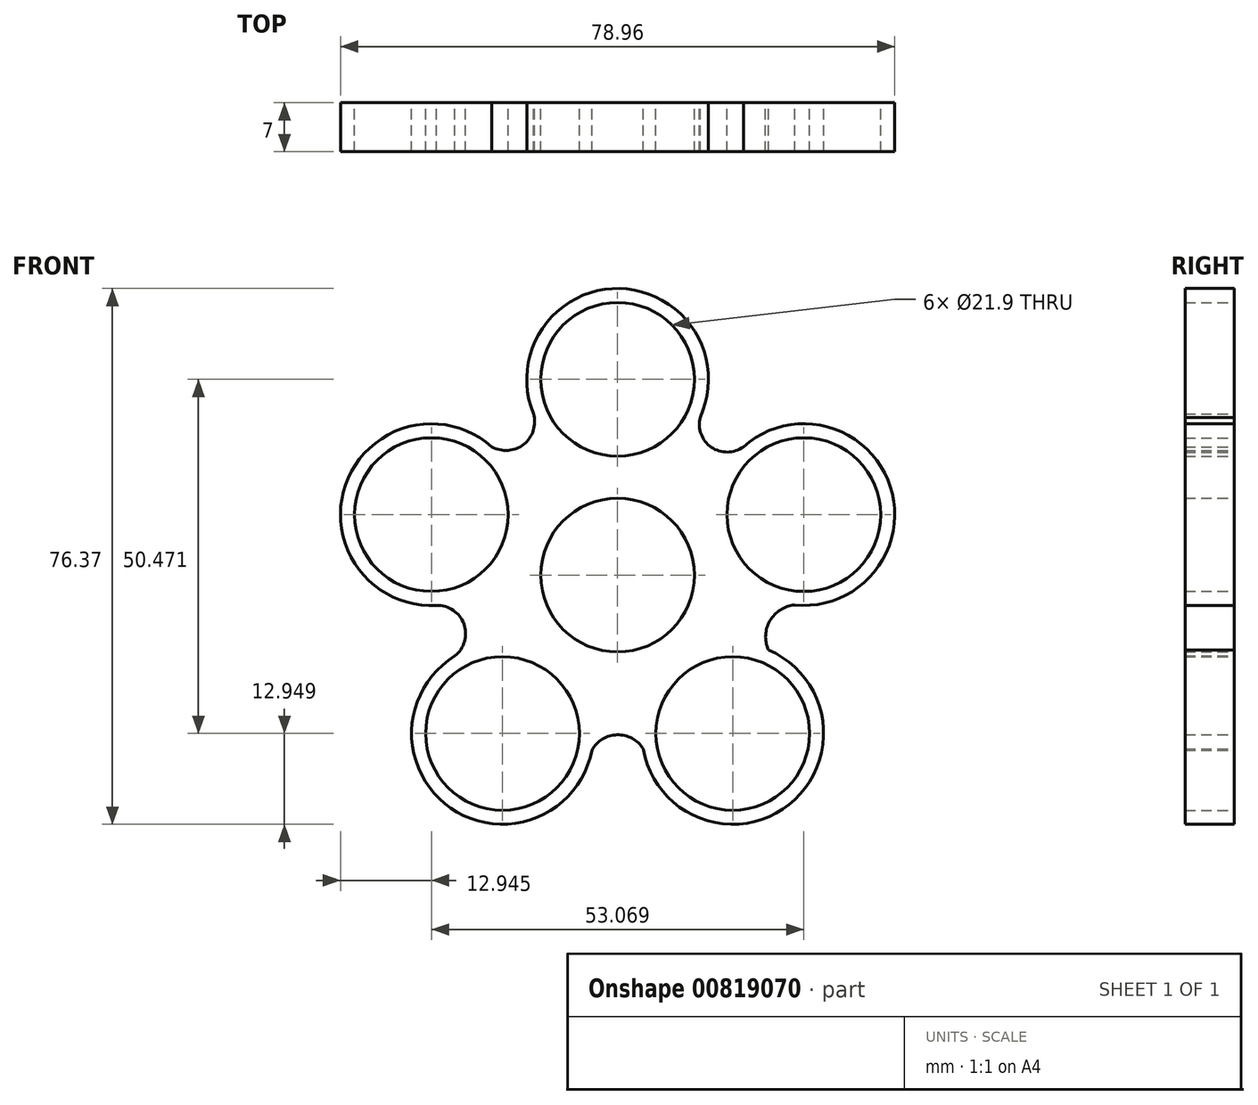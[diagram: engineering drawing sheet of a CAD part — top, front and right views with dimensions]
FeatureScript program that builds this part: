
annotation { "Feature Type Name" : "Feature", "Feature Type Description" : "" }
export const myFeature = defineFeature(function(context is Context, id is Id, definition is map)
    precondition{}
    {
        {
            var Q0;
            Q0=qCreatedBy(makeId("Front.planeOp"),FACE);
            var sketch = newSketch(context, id + "F0", { "sketchPlane" : qUnion([Q0])});
            skCircle(sketch, "E0", {"center": v(0, 0) * mm, "radius": 10.95 * mm});
            skCircle(sketch, "E1.0", {"center": v(0, 0) * mm, "radius": 12.95 * mm});
            skCircle(sketch, "E2", {"center": v(0, 27.9) * mm, "radius": 10.95 * mm});
            skCircle(sketch, "E3.0", {"center": v(0, 27.9) * mm, "radius": 12.95 * mm});
            skCircle(sketch, "E4.1.0", {"center": v(-26.53, 8.62) * mm, "radius": 12.95 * mm});
            skCircle(sketch, "E4.1.1", {"center": v(-26.53, 8.62) * mm, "radius": 10.95 * mm});
            skCircle(sketch, "E4.2.0", {"center": v(-16.4, -22.57) * mm, "radius": 12.95 * mm});
            skCircle(sketch, "E4.2.1", {"center": v(-16.4, -22.57) * mm, "radius": 10.95 * mm});
            skCircle(sketch, "E4.3.0", {"center": v(16.4, -22.57) * mm, "radius": 12.95 * mm});
            skCircle(sketch, "E4.3.1", {"center": v(16.4, -22.57) * mm, "radius": 10.95 * mm});
            skCircle(sketch, "E4.4.0", {"center": v(26.53, 8.62) * mm, "radius": 12.95 * mm});
            skCircle(sketch, "E4.4.1", {"center": v(26.53, 8.62) * mm, "radius": 10.95 * mm});
            skPoint(sketch, "E5.endSnap0", {"position": v(21.47, -6.97) * mm});
            skArc(sketch, "E6", {"start": v(12.17, 23.48) * mm, "mid": v(12.95, 18.56) * mm, "end": v(17.93, 18.3) * mm});
            skPoint(sketch, "E6.midSnap0", {"position": v(13.3, 18.3) * mm});
            skPoint(sketch, "E6.midSnap1", {"position": v(13.27, 4.31) * mm});
            skPoint(sketch, "E6.endSnap0", {"position": v(13.3, 18.3) * mm});
            skArc(sketch, "E7", {"start": v(26.53, -4.33) * mm, "mid": v(22.08, -5.96) * mm, "end": v(21.47, -10.65) * mm});
            skArc(sketch, "E8", {"start": v(4.26, -27.09) * mm, "mid": v(0.16, -22.76) * mm, "end": v(-4.18, -26.86) * mm});
            skArc(sketch, "E9", {"start": v(-23.82, -11.96) * mm, "mid": v(-21.79, -7.35) * mm, "end": v(-25.8, -4.3) * mm});
            skArc(sketch, "E10", {"start": v(-17.93, 18.3) * mm, "mid": v(-13.13, 18.85) * mm, "end": v(-12.22, 23.6) * mm});
            skSolve(sketch);
        }
        {
            var Q0;
            Q0 = qSketchRegion(id + "F0", true);
            var Q1;
            Q1=makeQuery(id+"F0.imprint","IMPRINT",FACE,{"disambiguationData":[TD([[makeQuery(id+"F0.imprint","IMPRINT",EDGE,{"derivedFrom":sQuery(id+"F0.wireOp",EDGE,"E0")}),-1.0]])]});
            extrude(context, id + "F1", {"entities" : qUnion([Q0, Q1]), "depth" : 7 * mm, "offsetDistance" : 25 * mm});
        }
    });
